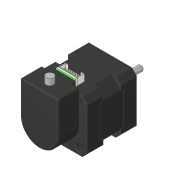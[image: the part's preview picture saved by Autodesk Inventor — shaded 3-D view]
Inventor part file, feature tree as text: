
AUTODESK INVENTOR PART (.ipt)
format: ipt  version: 2018 (Build 220112000, 112)  size: 355,840 bytes
history: native  units: in
note: dims shown in document units (in); Inventor stores cm internally (conversion verified against a paired STEP export)
features: extrude x5, sketch x5, chamfer x1, fillet x1, projected_geometry x1, other x1
ambient origin geometry x8: Origin, YZ Plane, XZ Plane, XY Plane, X Axis, Y Axis, Z Axis, Center Point
bodies: Solid1 (feature_tree)
feature tree (14):
  extrude  "Extrusion1"  Depth=0.3937in TaperAngle=0.0deg
  extrude  "Extrusion2"  Depth=0.0197in TaperAngle=45.0deg
  extrude  "Extrusion3"  Depth=1.0236in
  chamfer  "Chamfer1"  Distance=0.6693in
  extrude  "Extrusion4"  Depth=0.2362in
  fillet  "Fillet1"  Radius=0.1969in
  extrude  "Extrusion5"  [1 undecoded]
  sketch  "Sketch1"  dims[d0=0.3937in d1=0.0in d2=0.3937in d3=0.0in]
  sketch  "Sketch2"  dims[d4=0.0394in d5=0.0in d6=0.0197in d7=0.0787in d8=45.0deg]
  sketch  "Sketch3"  dims[d9=1.1811in d10=1.0236in d11=0.6693in d12=0.0in]
  projected_geometry  "Projected Loop1"
  sketch  "Sketch4"  dims[d13=0.0394in d14=0.2362in d15=0.1969in d16=0.0in]
  sketch  "Sketch5"
  other  "Filete1"
note: 1 required parameter value undecoded (feature->parameter linkage not recoverable at this tier; creation-order binding heuristic only, values carry confidence <= 0.55)
